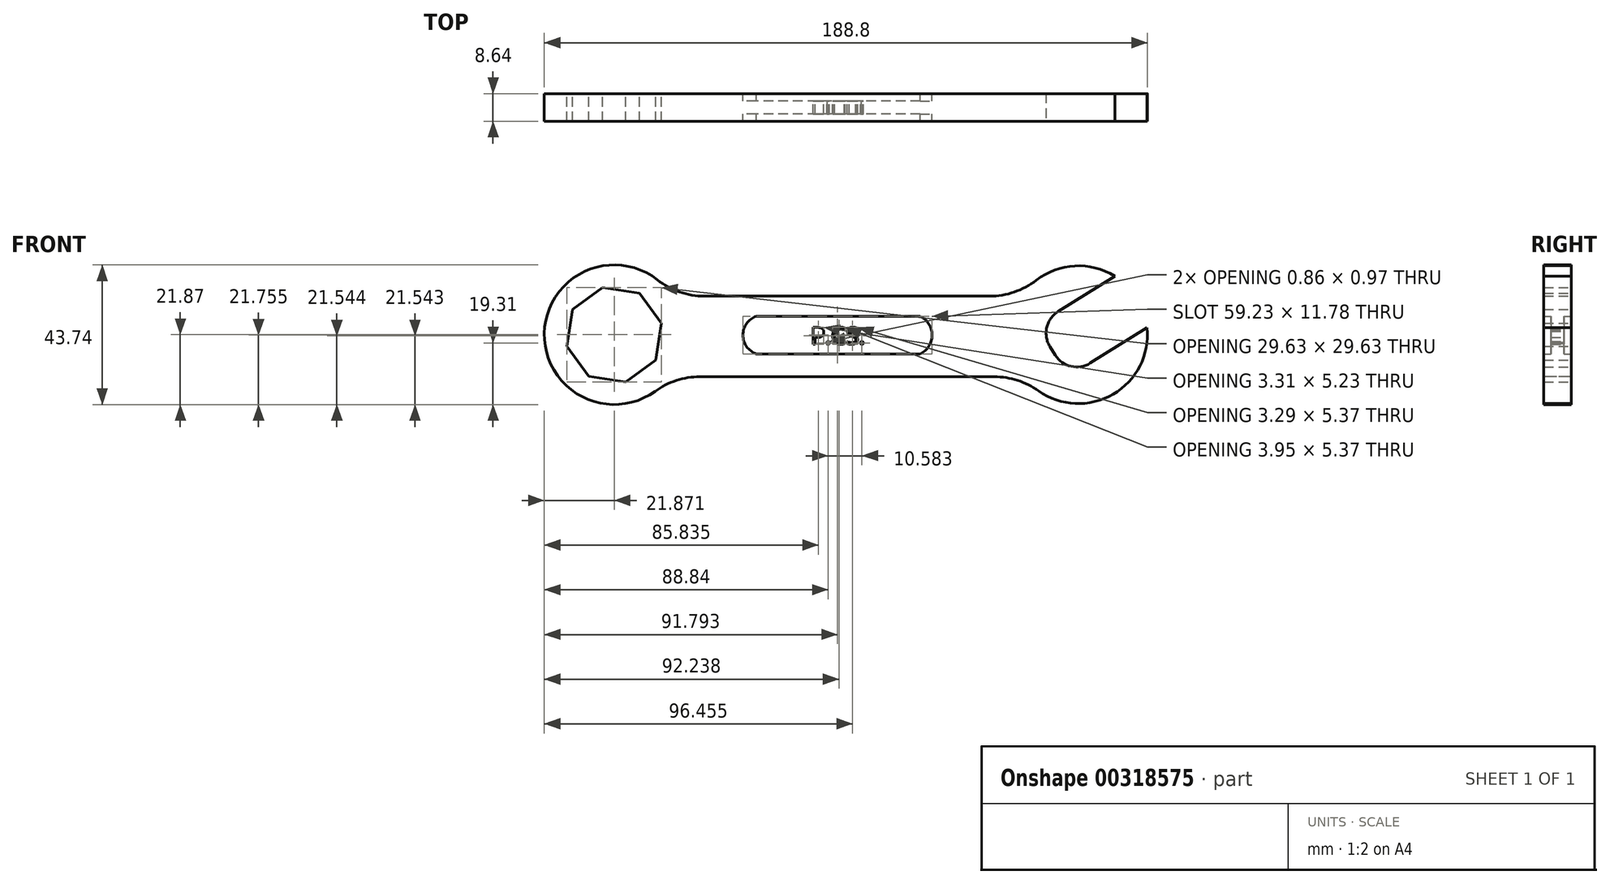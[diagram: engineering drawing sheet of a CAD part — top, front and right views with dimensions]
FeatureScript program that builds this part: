
annotation { "Feature Type Name" : "Feature", "Feature Type Description" : "" }
export const myFeature = defineFeature(function(context is Context, id is Id, definition is map)
    precondition{}
    {
        {
            var Q0;
            Q0=qCreatedBy(makeId("Front.planeOp"),FACE);
            var sketch = newSketch(context, id + "F0", { "sketchPlane" : qUnion([Q0])});
            skCircle(sketch, "E0", {"center": v(-64.46, 0) * mm, "radius": 21.87 * mm});
            skArc(sketch, "E1", {"start": v(92.25, 18.35) * mm, "mid": v(62.6, -11.46) * mm, "end": v(102.36, 2.2) * mm});
            skLineSegment(sketch, "E2", {"start": v(-46.23, 12.09) * mm, "end": v(63, 12.09) * mm});
            skLineSegment(sketch, "E3", {"start": v(-47, -13.18) * mm, "end": v(63.8, -13.18) * mm});
            skCircle(sketch, "E4.cCircle", {"center": v(-64.46, 0) * mm, "radius": 15.24 * mm, "construction": true});
            skLineSegment(sketch, "E4.0", {"start": v(-49.65, 3.58) * mm, "end": v(-51.45, -7.94) * mm});
            skLineSegment(sketch, "E4.1", {"start": v(-51.45, -7.94) * mm, "end": v(-60.88, -14.81) * mm});
            skLineSegment(sketch, "E4.2", {"start": v(-60.88, -14.81) * mm, "end": v(-72.4, -13) * mm});
            skLineSegment(sketch, "E4.3", {"start": v(-72.4, -13) * mm, "end": v(-79.27, -3.58) * mm});
            skLineSegment(sketch, "E4.4", {"start": v(-79.27, -3.58) * mm, "end": v(-77.47, 7.94) * mm});
            skLineSegment(sketch, "E4.5", {"start": v(-77.47, 7.94) * mm, "end": v(-68.04, 14.81) * mm});
            skLineSegment(sketch, "E4.6", {"start": v(-68.04, 14.81) * mm, "end": v(-56.52, 13) * mm});
            skLineSegment(sketch, "E4.7", {"start": v(-56.52, 13) * mm, "end": v(-49.65, 3.58) * mm});
            skCircle(sketch, "E5.cCircle", {"center": v(80.89, 0) * mm, "radius": 9.53 * mm, "construction": true});
            skLineSegment(sketch, "E5.1", {"start": v(94.02, -3.02) * mm, "end": v(77.87, -13.13) * mm});
            skLineSegment(sketch, "E5.2", {"start": v(77.87, -13.13) * mm, "end": v(67.76, 3.02) * mm});
            skLineSegment(sketch, "E5.3", {"start": v(67.76, 3.02) * mm, "end": v(83.9, 13.13) * mm});
            skLineSegment(sketch, "E6", {"start": v(94.02, -3.02) * mm, "end": v(102.36, 2.2) * mm});
            skLineSegment(sketch, "E7", {"start": v(83.9, 13.13) * mm, "end": v(92.25, 18.35) * mm});
            skLineSegment(sketch, "E8", {"start": v(31.32, 5.77) * mm, "end": v(-19.95, 5.77) * mm});
            skLineSegment(sketch, "E9", {"start": v(-19.95, -6) * mm, "end": v(31.32, -6) * mm});
            skArc(sketch, "E10", {"start": v(-19.95, 5.77) * mm, "mid": v(-24.15, -0.11) * mm, "end": v(-19.95, -6) * mm});
            skArc(sketch, "E11", {"start": v(31.32, -6) * mm, "mid": v(35.08, -0.11) * mm, "end": v(31.32, 5.77) * mm});
            skText(sketch, "E12", { "text": "P.CS.", "fontName": "OpenSans-Regular.ttf"});
            const initialGuessF0  = {"E12": [-0.00287, -0.00294, 1, 0, 0.00527]};
            skSetInitialGuess(sketch, initialGuessF0);
            skSolve(sketch);
        }
        {
            var Q0;
            {var subQ0=sQuery(id+"F0.wireOp",EDGE,"E2");Q0=makeQuery(id+"F0.imprint","IMPRINT",FACE,{"disambiguationData":[TD([[makeQuery(id+"F0.imprint","IMPRINT",EDGE,{"derivedFrom":subQ0}),-1.0]])]});}
            var Q1;
            Q1=makeQuery(id+"F0.imprint","IMPRINT",FACE,{"disambiguationData":[TD([[makeQuery(id+"F0.imprint","IMPRINT",EDGE,{"derivedFrom":sQuery(id+"F0.wireOp",EDGE,"E5.1")}),1.0]])]});
            var Q2;
            Q2=makeQuery(id+"F0.imprint","IMPRINT",FACE,{"disambiguationData":[TD([[makeQuery(id+"F0.imprint","IMPRINT",EDGE,{"derivedFrom":sQuery(id+"F0.wireOp",EDGE,"E4.0")}),1.0]])]});
            extrude(context, id + "F1", {"entities" : qUnion([Q0, Q1, Q2]), "endBound" : BoundingType.SYMMETRIC, "depth" : 8.64 * mm});
        }
        {
            var Q0;
            Q0=makeQuery(id+"F0.imprint","IMPRINT",FACE,{"disambiguationData":[TD([[makeQuery(id+"F0.imprint","IMPRINT",EDGE,{"derivedFrom":sQuery(id+"F0.wireOp",EDGE,"E8")}),1.0]])]});
            extrude(context, id + "F2", {"entities" : qUnion([Q0]), "operationType" : NewBodyOperationType.ADD, "endBound" : BoundingType.SYMMETRIC, "depth" : 4.06 * mm});
        }
        {
            var Q0;
            Q0=makeQuery(id+"F1.opExtrude","SWEPT_EDGE",EDGE,{"disambiguationData":[OSD([sQuery(id+"F0.wireOp",EDGE,"E5.2"),sQuery(id+"F0.wireOp",EDGE,"E5.3")])]});
            var Q1;
            Q1=makeQuery(id+"F1.opExtrude","SWEPT_EDGE",EDGE,{"disambiguationData":[OSD([sQuery(id+"F0.wireOp",EDGE,"E5.1"),sQuery(id+"F0.wireOp",EDGE,"E5.2")])]});
            fillet(context, id + "F3", {"entities" : qUnion([Q0, Q1]), "radius" : 7.97 * mm, "tangentPropagation" : true, "allowEdgeOverflow" : false});
        }
        {
            var Q0;
            Q0=makeQuery(id+"F1.opExtrude","SWEPT_EDGE",EDGE,{"disambiguationData":[OSD([sQuery(id+"F0.wireOp",EDGE,"E1"),sQuery(id+"F0.wireOp",EDGE,"E2")])]});
            var Q1;
            Q1=makeQuery(id+"F1.opExtrude","SWEPT_EDGE",EDGE,{"disambiguationData":[OSD([sQuery(id+"F0.wireOp",EDGE,"E0"),sQuery(id+"F0.wireOp",EDGE,"E2")])]});
            var Q2;
            Q2=makeQuery(id+"F1.opExtrude","SWEPT_EDGE",EDGE,{"disambiguationData":[OSD([sQuery(id+"F0.wireOp",EDGE,"E1"),sQuery(id+"F0.wireOp",EDGE,"E3")])]});
            var Q3;
            Q3=makeQuery(id+"F1.opExtrude","SWEPT_EDGE",EDGE,{"disambiguationData":[OSD([sQuery(id+"F0.wireOp",EDGE,"E0"),sQuery(id+"F0.wireOp",EDGE,"E3")])]});
            fillet(context, id + "F4", {"entities" : qUnion([Q0, Q1, Q2, Q3]), "radius" : 23.86 * mm, "tangentPropagation" : true, "allowEdgeOverflow" : false});
        }
    });
